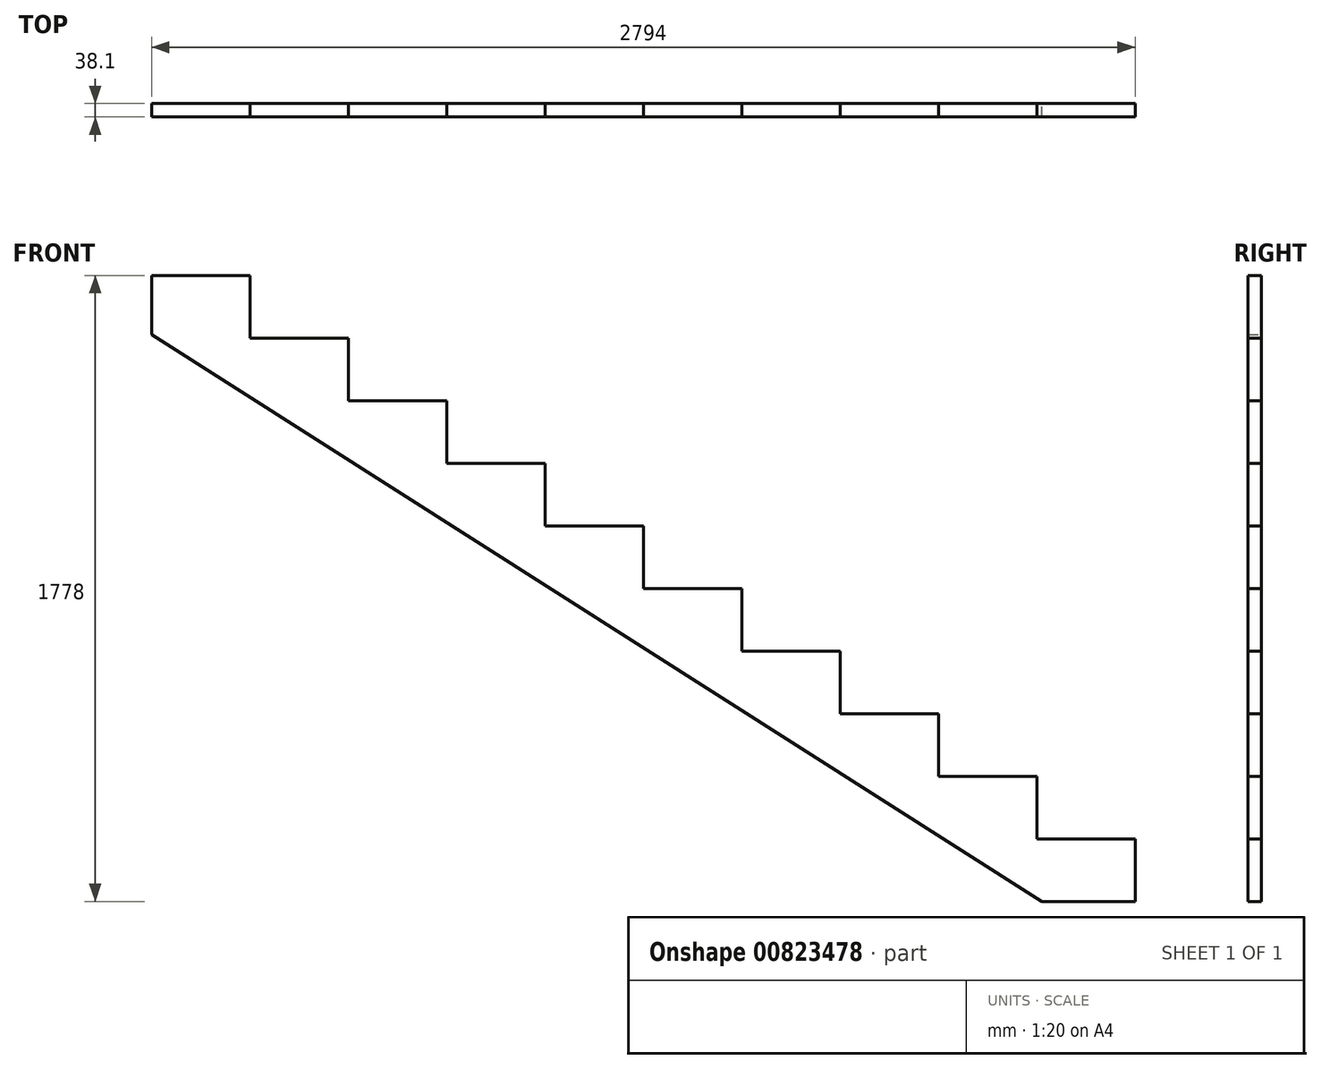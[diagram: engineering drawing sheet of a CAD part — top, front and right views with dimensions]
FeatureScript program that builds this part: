
annotation { "Feature Type Name" : "Feature", "Feature Type Description" : "" }
export const myFeature = defineFeature(function(context is Context, id is Id, definition is map)
    precondition{}
    {
        {
            var Q0;
            Q0=qCreatedBy(makeId("Front.planeOp"),FACE);
            var sketch = newSketch(context, id + "F0", { "sketchPlane" : qUnion([Q0])});
            skLineSegment(sketch, "E0", {"start": v(0, 0) * mm, "end": v(279.4, 0) * mm});
            skLineSegment(sketch, "E1", {"start": v(279.4, 0) * mm, "end": v(279.4, -177.8) * mm});
            skLineSegment(sketch, "E2", {"start": v(279.4, -177.8) * mm, "end": v(558.8, -177.8) * mm});
            skLineSegment(sketch, "E3", {"start": v(0, 0) * mm, "end": v(0, -168.43) * mm});
            skLineSegment(sketch, "E4", {"start": v(0, -168.43) * mm, "end": v(2529.33, -1778) * mm});
            skLineSegment(sketch, "E5", {"start": v(558.8, -177.8) * mm, "end": v(558.8, -355.6) * mm});
            skLineSegment(sketch, "E6", {"start": v(558.8, -355.6) * mm, "end": v(838.2, -355.6) * mm});
            skLineSegment(sketch, "E7", {"start": v(838.2, -355.6) * mm, "end": v(838.2, -533.4) * mm});
            skLineSegment(sketch, "E8", {"start": v(838.2, -533.4) * mm, "end": v(1117.6, -533.4) * mm});
            skLineSegment(sketch, "E9", {"start": v(1117.6, -533.4) * mm, "end": v(1117.6, -711.2) * mm});
            skLineSegment(sketch, "E10", {"start": v(1117.6, -711.2) * mm, "end": v(1397, -711.2) * mm});
            skLineSegment(sketch, "E11", {"start": v(1397, -711.2) * mm, "end": v(1397, -889) * mm});
            skLineSegment(sketch, "E12", {"start": v(1397, -889) * mm, "end": v(1676.4, -889) * mm});
            skLineSegment(sketch, "E13", {"start": v(1676.4, -889) * mm, "end": v(1676.4, -1066.8) * mm});
            skLineSegment(sketch, "E14", {"start": v(1676.4, -1066.8) * mm, "end": v(1955.8, -1066.8) * mm});
            skLineSegment(sketch, "E15", {"start": v(1955.8, -1066.8) * mm, "end": v(1955.8, -1244.6) * mm});
            skLineSegment(sketch, "E16", {"start": v(1955.8, -1244.6) * mm, "end": v(2235.2, -1244.6) * mm});
            skLineSegment(sketch, "E17", {"start": v(2235.2, -1244.6) * mm, "end": v(2235.2, -1422.4) * mm});
            skLineSegment(sketch, "E18", {"start": v(2235.2, -1422.4) * mm, "end": v(2514.6, -1422.4) * mm});
            skLineSegment(sketch, "E19", {"start": v(2514.6, -1422.4) * mm, "end": v(2514.6, -1600.2) * mm});
            skLineSegment(sketch, "E20", {"start": v(2514.6, -1600.2) * mm, "end": v(2794, -1600.2) * mm});
            skLineSegment(sketch, "E21", {"start": v(2794, -1600.2) * mm, "end": v(2794, -1778) * mm});
            skLineSegment(sketch, "E22", {"start": v(2794, -1778) * mm, "end": v(2529.33, -1778) * mm});
            skLineSegment(sketch, "E23", {"start": v(279.4, 0) * mm, "end": v(2794, -1600.2) * mm, "construction": true});
            skSolve(sketch);
        }
        {
            var Q0;
            Q0 = qSketchRegion(id + "F0", true);
            extrude(context, id + "F1", {"entities" : qUnion([Q0]), "depth" : 38.1 * mm, "offsetDistance" : 25.4 * mm});
        }
    });
